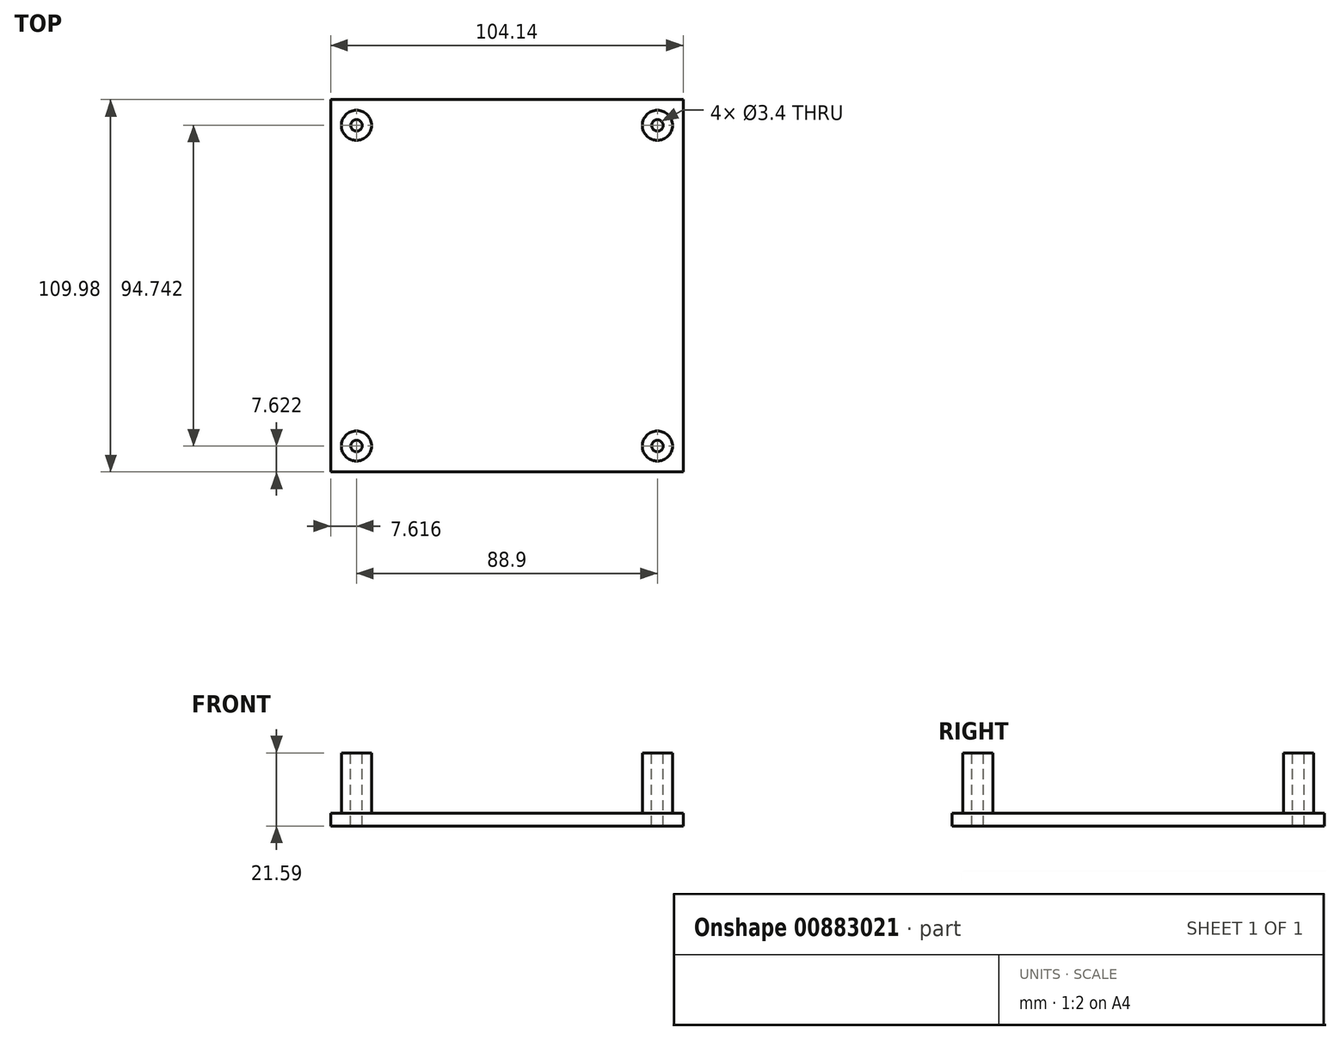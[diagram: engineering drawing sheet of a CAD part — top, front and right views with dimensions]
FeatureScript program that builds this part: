
annotation { "Feature Type Name" : "Feature", "Feature Type Description" : "" }
export const myFeature = defineFeature(function(context is Context, id is Id, definition is map)
    precondition{}
    {
        {
            var Q0;
            Q0=qCreatedBy(makeId("Top.planeOp"),FACE);
            var sketch = newSketch(context, id + "F0", { "sketchPlane" : qUnion([Q0])});
            skLineSegment(sketch, "E0.bottom", {"start": v(-51.58, 63.16) * mm, "end": v(52.56, 63.16) * mm});
            skLineSegment(sketch, "E0.top", {"start": v(-51.58, -46.82) * mm, "end": v(52.56, -46.82) * mm});
            skLineSegment(sketch, "E0.left", {"start": v(-51.58, 63.16) * mm, "end": v(-51.58, -46.82) * mm});
            skLineSegment(sketch, "E0.right", {"start": v(52.56, 63.16) * mm, "end": v(52.56, -46.82) * mm});
            skSolve(sketch);
        }
        {
            var Q0;
            Q0=makeQuery(id+"F0.imprint","IMPRINT",FACE,{"disambiguationData":[TD([[makeQuery(id+"F0.imprint","IMPRINT",EDGE,{"derivedFrom":sQuery(id+"F0.wireOp",EDGE,"E0.bottom")}),-1.0]])]});
            extrude(context, id + "F1", {"entities" : qUnion([Q0]), "depth" : 3.8 * mm, "offsetDistance" : 25.4 * mm});
        }
        {
            var Q0;
            Q0=makeQuery(id+"F1.opExtrude","CAP_FACE",FACE,{"disambiguationData":[OSD([sQuery(id+"F0.wireOp",EDGE,"E0.bottom"),sQuery(id+"F0.wireOp",EDGE,"E0.top"),sQuery(id+"F0.wireOp",EDGE,"E0.left"),sQuery(id+"F0.wireOp",EDGE,"E0.right")])],"isStart":false});
            var sketch = newSketch(context, id + "F2", { "sketchPlane" : qUnion([Q0])});
            skCircle(sketch, "E1", {"center": v(-43.96, 55.54) * mm, "radius": 4.45 * mm});
            skCircle(sketch, "E2", {"center": v(44.94, 55.54) * mm, "radius": 4.45 * mm});
            skCircle(sketch, "E3", {"center": v(-43.96, -39.2) * mm, "radius": 4.45 * mm});
            skCircle(sketch, "E4", {"center": v(44.94, -39.2) * mm, "radius": 4.45 * mm});
            skSolve(sketch);
        }
        {
            var Q0;
            Q0=makeQuery(id+"F2.imprint","IMPRINT",FACE,{"disambiguationData":[TD([[makeQuery(id+"F2.imprint","IMPRINT",EDGE,{"derivedFrom":sQuery(id+"F2.wireOp",EDGE,"E1")}),1.0]])]});
            var Q1;
            Q1=makeQuery(id+"F2.imprint","IMPRINT",FACE,{"disambiguationData":[TD([[makeQuery(id+"F2.imprint","IMPRINT",EDGE,{"derivedFrom":sQuery(id+"F2.wireOp",EDGE,"E2")}),1.0]])]});
            var Q2;
            Q2=makeQuery(id+"F2.imprint","IMPRINT",FACE,{"disambiguationData":[TD([[makeQuery(id+"F2.imprint","IMPRINT",EDGE,{"derivedFrom":sQuery(id+"F2.wireOp",EDGE,"E3")}),1.0]])]});
            var Q3;
            Q3=makeQuery(id+"F2.imprint","IMPRINT",FACE,{"disambiguationData":[TD([[makeQuery(id+"F2.imprint","IMPRINT",EDGE,{"derivedFrom":sQuery(id+"F2.wireOp",EDGE,"E4")}),1.0]])]});
            extrude(context, id + "F3", {"entities" : qUnion([Q0, Q1, Q2, Q3]), "operationType" : NewBodyOperationType.ADD, "depth" : 17.78 * mm, "offsetDistance" : 25.4 * mm});
        }
        {
            var Q0;
            Q0=qCreatedBy(makeId("Top.planeOp"),FACE);
            cPlane(context, id + "F4", {"entities" : qUnion([Q0]), "cplaneType" : CPlaneType.OFFSET, "offset" : 21.59 * mm, "width" : 152.4 * mm, "height" : 152.4 * mm});
        }
        {
            var Q0;
            Q0=qCreatedBy(id+"F4.planeOp",FACE);
            var sketch = newSketch(context, id + "F5", { "sketchPlane" : qUnion([Q0])});
            skPoint(sketch, "E5", {"position": v(-43.96, 55.54) * mm});
            skPoint(sketch, "E6", {"position": v(44.94, 55.54) * mm});
            skPoint(sketch, "E7", {"position": v(-43.96, -39.2) * mm});
            skPoint(sketch, "E8", {"position": v(44.94, -39.2) * mm});
            skSolve(sketch);
        }
        {
            var Q0;
            Q0=sQuery(id+"F5.wireOp",VERTEX,"E5");
            var Q1;
            Q1=sQuery(id+"F5.wireOp",VERTEX,"E6");
            var Q2;
            Q2=sQuery(id+"F5.wireOp",VERTEX,"E7");
            var Q3;
            Q3=sQuery(id+"F5.wireOp",VERTEX,"E8");
            var Q4;
            Q4=makeQuery(id+"F1.opExtrude","SWEPT_BODY",BODY,{"disambiguationData":[OSD([sQuery(id+"F0.wireOp",EDGE,"E0.bottom"),sQuery(id+"F0.wireOp",EDGE,"E0.top"),sQuery(id+"F0.wireOp",EDGE,"E0.left"),sQuery(id+"F0.wireOp",EDGE,"E0.right")])]});
            hole(context, id + "F6", {"style" : HoleStyle.SIMPLE, "endStyle" : HoleEndStyle.THROUGH, "standardTappedOrClearance" : lookupTablePath({ "fit" : "Normal", "standard" : "ISO", "size" : "M3", "type" : "Clearance" }), "standardBlindInLast" : lookupTablePath({ "fit" : "Normal", "standard" : "ISO", "size" : "M3", "type" : "Clearance" }), "holeDiameter" : 3.4 * mm, "majorDiameter" : 6.35 * mm, "isTappedThrough" : true, "tappedDepth" : 12.7 * mm, "tapClearance" : 3, "locations" : qUnion([Q0, Q1, Q2, Q3]), "scope" : qUnion([Q4])});
        }
    });
